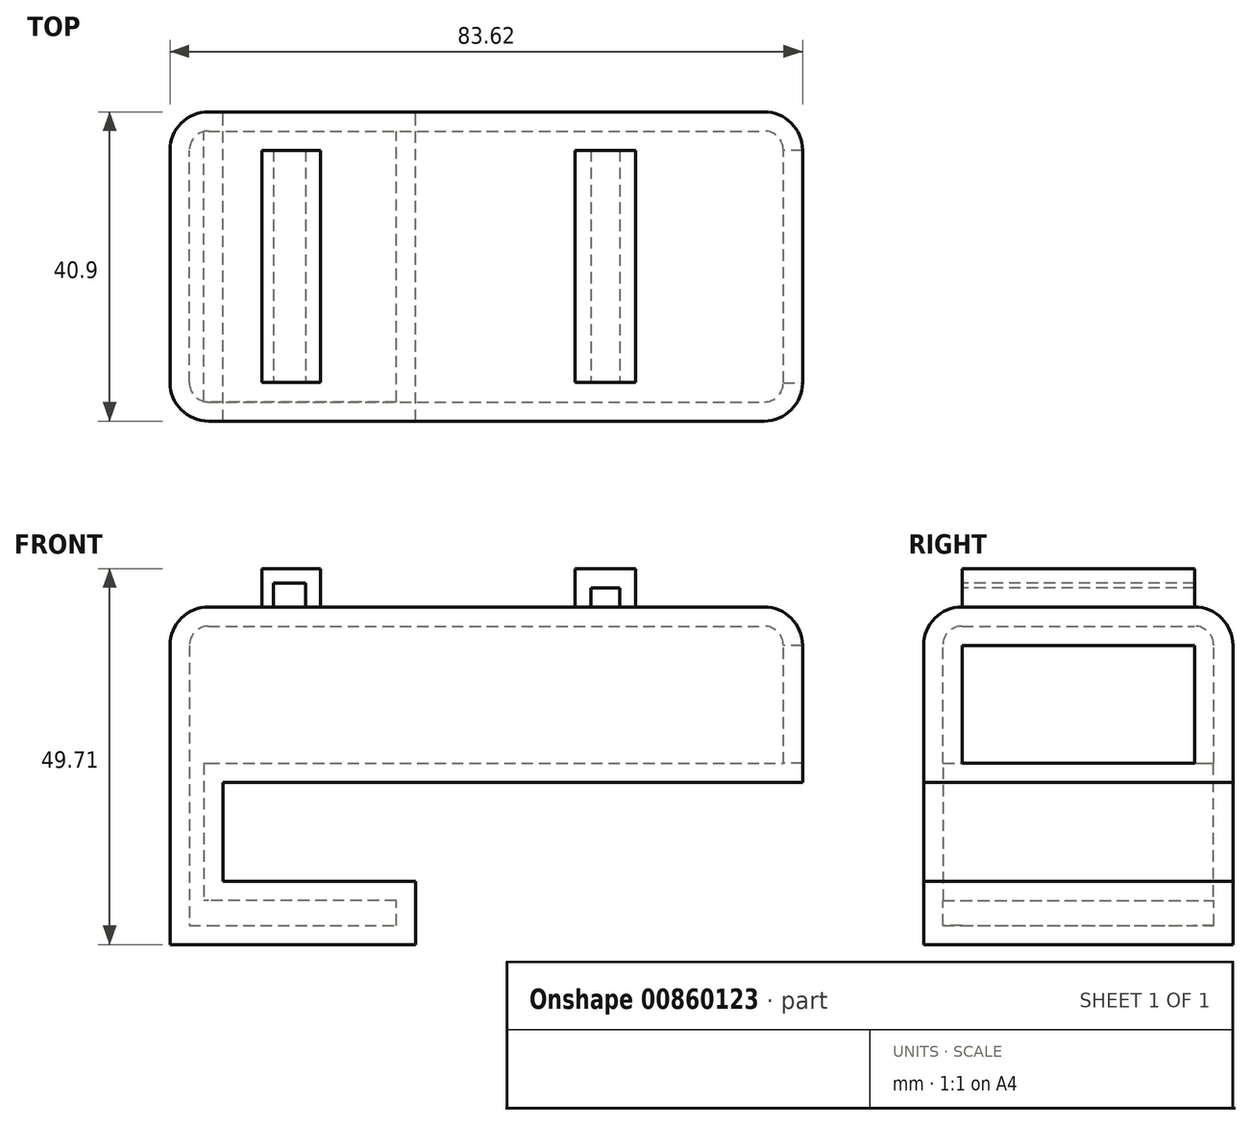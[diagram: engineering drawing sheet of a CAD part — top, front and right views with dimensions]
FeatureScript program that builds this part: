
annotation { "Feature Type Name" : "Feature", "Feature Type Description" : "" }
export const myFeature = defineFeature(function(context is Context, id is Id, definition is map)
    precondition{}
    {
        {
            var Q0;
            Q0=qCreatedBy(makeId("Front.planeOp"),FACE);
            var sketch = newSketch(context, id + "F0", { "sketchPlane" : qUnion([Q0])});
            skLineSegment(sketch, "E0.bottom", {"start": v(-38.09, 12.06) * mm, "end": v(45.53, 12.06) * mm});
            skLineSegment(sketch, "E0.top", {"start": v(-31.1, -11.16) * mm, "end": v(45.53, -11.16) * mm});
            skLineSegment(sketch, "E0.left", {"start": v(-38.09, 12.06) * mm, "end": v(-38.09, -11.16) * mm});
            skLineSegment(sketch, "E0.right", {"start": v(45.53, 12.06) * mm, "end": v(45.53, -11.16) * mm});
            skLineSegment(sketch, "E1", {"start": v(-38.09, -11.16) * mm, "end": v(-38.09, -32.57) * mm});
            skLineSegment(sketch, "E2", {"start": v(-38.09, -32.57) * mm, "end": v(-5.63, -32.57) * mm});
            skLineSegment(sketch, "E3", {"start": v(-5.63, -32.57) * mm, "end": v(-5.63, -24.23) * mm});
            skLineSegment(sketch, "E4", {"start": v(-5.63, -24.23) * mm, "end": v(-31.1, -24.23) * mm});
            skLineSegment(sketch, "E5", {"start": v(-31.1, -24.23) * mm, "end": v(-31.1, -11.16) * mm});
            skSolve(sketch);
        }
        {
            var Q0;
            Q0=makeQuery(id+"F0.imprint","IMPRINT",FACE,{"disambiguationData":[TD([[makeQuery(id+"F0.imprint","IMPRINT",EDGE,{"derivedFrom":sQuery(id+"F0.wireOp",EDGE,"E0.bottom")}),-1.0]])]});
            extrude(context, id + "F1", {"entities" : qUnion([Q0]), "depth" : 40.9 * mm, "offsetDistance" : 25.4 * mm});
        }
        {
            var Q0;
            Q0=makeQuery(id+"F1.opExtrude","CAP_EDGE",EDGE,{"disambiguationData":[OSD([sQuery(id+"F0.wireOp",EDGE,"E0.right")])],"isStart":true});
            var Q1;
            Q1=makeQuery(id+"F1.opExtrude","CAP_EDGE",EDGE,{"disambiguationData":[OSD([sQuery(id+"F0.wireOp",EDGE,"E0.right")])],"isStart":false});
            var Q2;
            Q2=makeQuery(id+"F1.opExtrude","CAP_EDGE",EDGE,{"disambiguationData":[OSD([sQuery(id+"F0.wireOp",EDGE,"E0.left"),sQuery(id+"F0.wireOp",EDGE,"E1")])],"isStart":true});
            var Q3;
            Q3=makeQuery(id+"F1.opExtrude","CAP_EDGE",EDGE,{"disambiguationData":[OSD([sQuery(id+"F0.wireOp",EDGE,"E0.bottom")])],"isStart":true});
            var Q4;
            Q4=makeQuery(id+"F1.opExtrude","CAP_EDGE",EDGE,{"disambiguationData":[OSD([sQuery(id+"F0.wireOp",EDGE,"E0.bottom")])],"isStart":false});
            var Q5;
            Q5=makeQuery(id+"F1.opExtrude","SWEPT_EDGE",EDGE,{"disambiguationData":[OSD([sQuery(id+"F0.wireOp",EDGE,"E0.bottom"),sQuery(id+"F0.wireOp",EDGE,"E0.right")])]});
            var Q6;
            Q6=makeQuery(id+"F1.opExtrude","SWEPT_EDGE",EDGE,{"disambiguationData":[OSD([sQuery(id+"F0.wireOp",EDGE,"E0.bottom"),sQuery(id+"F0.wireOp",EDGE,"E0.left")])]});
            fillet(context, id + "F2", {"entities" : qUnion([Q0, Q1, Q2, Q3, Q4, Q5, Q6]), "radius" : 5.08 * mm, "tangentPropagation" : true, "allowEdgeOverflow" : false});
        }
        {
            var Q0;
            Q0=makeQuery(id+"F1.opExtrude","CAP_EDGE",EDGE,{"disambiguationData":[OSD([sQuery(id+"F0.wireOp",EDGE,"E0.left"),sQuery(id+"F0.wireOp",EDGE,"E1")])],"isStart":false});
            fillet(context, id + "F3", {"entities" : qUnion([Q0]), "radius" : 5.08 * mm, "tangentPropagation" : true, "allowEdgeOverflow" : false});
        }
        {
            var Q0;
            Q0=makeQuery(id+"F1.opExtrude","SWEPT_FACE",FACE,{"disambiguationData":[OSD([sQuery(id+"F0.wireOp",EDGE,"E0.bottom")])]});
            var sketch = newSketch(context, id + "F4", { "sketchPlane" : qUnion([Q0])});
            skLineSegment(sketch, "E6.bottom", {"start": v(-25.95, -35.81) * mm, "end": v(-18.22, -35.81) * mm});
            skLineSegment(sketch, "E6.top", {"start": v(-25.95, -5.08) * mm, "end": v(-18.22, -5.08) * mm});
            skLineSegment(sketch, "E6.left", {"start": v(-25.95, -35.81) * mm, "end": v(-25.95, -5.08) * mm});
            skLineSegment(sketch, "E6.right", {"start": v(-18.22, -35.81) * mm, "end": v(-18.22, -5.08) * mm});
            skLineSegment(sketch, "E7.bottom", {"start": v(15.47, -35.81) * mm, "end": v(23.46, -35.81) * mm});
            skLineSegment(sketch, "E7.top", {"start": v(15.47, -5.08) * mm, "end": v(23.46, -5.08) * mm});
            skLineSegment(sketch, "E7.left", {"start": v(15.47, -35.81) * mm, "end": v(15.47, -5.08) * mm});
            skLineSegment(sketch, "E7.right", {"start": v(23.46, -35.81) * mm, "end": v(23.46, -5.08) * mm});
            skSolve(sketch);
        }
        {
            var Q0;
            Q0=makeQuery(id+"F4.imprint","IMPRINT",FACE,{"disambiguationData":[TD([[makeQuery(id+"F4.imprint","IMPRINT",EDGE,{"derivedFrom":sQuery(id+"F4.wireOp",EDGE,"E6.bottom")}),1.0]])]});
            var Q1;
            Q1=makeQuery(id+"F4.imprint","IMPRINT",FACE,{"disambiguationData":[TD([[makeQuery(id+"F4.imprint","IMPRINT",EDGE,{"derivedFrom":sQuery(id+"F4.wireOp",EDGE,"E7.bottom")}),1.0]])]});
            extrude(context, id + "F5", {"entities" : qUnion([Q0, Q1]), "operationType" : NewBodyOperationType.ADD, "depth" : 5.08 * mm, "offsetDistance" : 25.4 * mm});
        }
        {
            var Q0;
            Q0=makeQuery(id+"F5.opExtrude","SWEPT_FACE",FACE,{"disambiguationData":[OSD([sQuery(id+"F4.wireOp",EDGE,"E6.bottom")])]});
            var sketch = newSketch(context, id + "F6", { "sketchPlane" : qUnion([Q0])});
            skLineSegment(sketch, "E8.bottom", {"start": v(-24.42, 12.06) * mm, "end": v(-20.17, 12.06) * mm});
            skLineSegment(sketch, "E8.top", {"start": v(-24.42, 15.22) * mm, "end": v(-20.17, 15.22) * mm});
            skLineSegment(sketch, "E8.left", {"start": v(-24.42, 12.06) * mm, "end": v(-24.42, 15.22) * mm});
            skLineSegment(sketch, "E8.right", {"start": v(-20.17, 12.06) * mm, "end": v(-20.17, 15.22) * mm});
            skPoint(sketch, "E9.oppositeSnap0", {"position": v(-18.22, 14.6) * mm});
            skLineSegment(sketch, "E9.bottom", {"start": v(17.52, 12.06) * mm, "end": v(21.37, 12.06) * mm});
            skLineSegment(sketch, "E9.top", {"start": v(17.52, 14.6) * mm, "end": v(21.37, 14.6) * mm});
            skLineSegment(sketch, "E9.left", {"start": v(17.52, 12.06) * mm, "end": v(17.52, 14.6) * mm});
            skLineSegment(sketch, "E9.right", {"start": v(21.37, 12.06) * mm, "end": v(21.37, 14.6) * mm});
            skSolve(sketch);
        }
        {
            var Q0;
            Q0=makeQuery(id+"F6.imprint","IMPRINT",FACE,{"disambiguationData":[TD([[makeQuery(id+"F6.imprint","IMPRINT",EDGE,{"derivedFrom":sQuery(id+"F6.wireOp",EDGE,"E8.bottom")}),1.0]])]});
            var Q1;
            Q1=makeQuery(id+"F6.imprint","IMPRINT",FACE,{"disambiguationData":[TD([[makeQuery(id+"F6.imprint","IMPRINT",EDGE,{"derivedFrom":sQuery(id+"F6.wireOp",EDGE,"E9.bottom")}),1.0]])]});
            extrude(context, id + "F7", {"entities" : qUnion([Q0, Q1]), "operationType" : NewBodyOperationType.REMOVE, "oppositeDirection" : true, "depth" : 39.37 * mm, "offsetDistance" : 25.4 * mm});
        }
        {
            var Q0;
            Q0=makeQuery(id+"F1.opExtrude","SWEPT_FACE",FACE,{"disambiguationData":[OSD([sQuery(id+"F0.wireOp",EDGE,"E0.right")])]});
            shell(context, id + "F8", {"entities" : qUnion([Q0]), "thickness" : 2.54 * mm});
        }
    });
